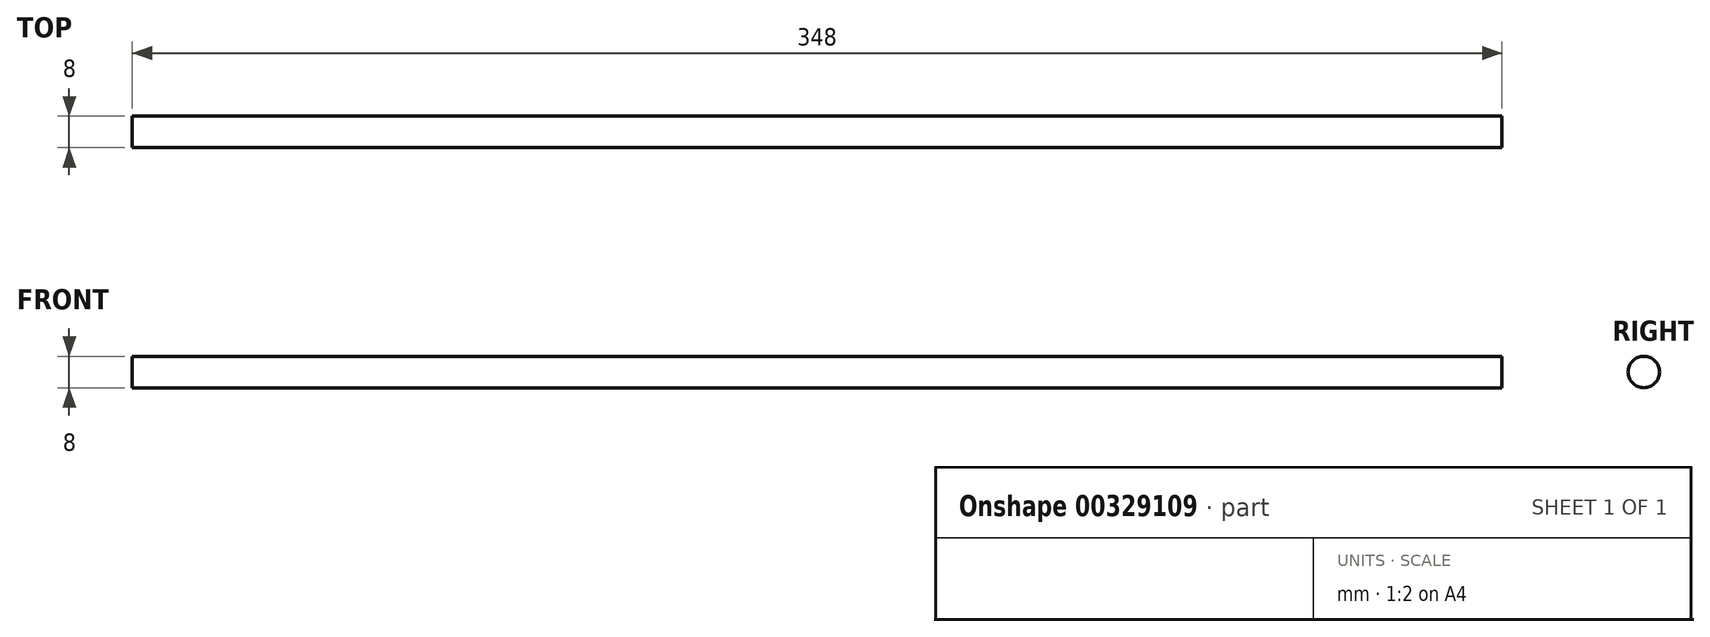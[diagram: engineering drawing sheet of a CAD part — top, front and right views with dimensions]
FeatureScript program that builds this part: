
annotation { "Feature Type Name" : "Feature", "Feature Type Description" : "" }
export const myFeature = defineFeature(function(context is Context, id is Id, definition is map)
    precondition{}
    {
        {
            var Q0;
            Q0=qCreatedBy(makeId("Right.planeOp"),FACE);
            var sketch = newSketch(context, id + "F0", { "sketchPlane" : qUnion([Q0])});
            skCircle(sketch, "E0", {"center": v(0, 0) * mm, "radius": 4 * mm});
            skSolve(sketch);
        }
        {
            var Q0;
            Q0 = qSketchRegion(id + "F0", true);
            extrude(context, id + "F1", {"entities" : qUnion([Q0]), "depth" : 348 * mm});
        }
    });
